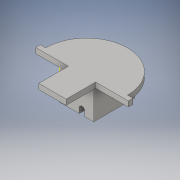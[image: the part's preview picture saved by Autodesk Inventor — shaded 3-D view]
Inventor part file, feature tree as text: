
AUTODESK INVENTOR PART (.ipt)
format: ipt  version: 2016 (Build 200138000, 138)  size: 614,912 bytes
history: native  units: in
note: dims shown in document units (in); Inventor stores cm internally (conversion verified against a paired STEP export)
features: reference x41, extrude x33, sketch x33, plane x6, projected_geometry x5
ambient origin geometry x8: Origin, YZ Plane, XZ Plane, XY Plane, X Axis, Y Axis, Z Axis, Center Point
bodies: Solid1 (feature_tree)
feature tree (118):
  extrude  "Extrusion1"  Depth=3.0in
  extrude  "Extrusion2"  Depth=0.1969in
  extrude  "Extrusion3"  Depth=1.0827in
  extrude  "Extrusion5"  Depth=1.0in TaperAngle=0.0deg
  plane  "Work Plane1"
  extrude  "Extrusion6"  Depth=0.0098in
  extrude  "Extrusion9"  Depth=0.1575in
  extrude  "Extrusion14"  Depth=0.1575in
  extrude  "Extrusion15"  Depth=1.25in
  plane  "Work Plane2"
  extrude  "Extrusion16"  Depth=0.1575in
  extrude  "Extrusion17"  Depth=0.1181in TaperAngle=0.0deg
  extrude  "Extrusion18"  Depth=0.1969in
  plane  "Work Plane3"
  extrude  "Extrusion20"  Depth=0.1969in TaperAngle=0.0deg
  extrude  "Extrusion21"  Depth=0.1181in TaperAngle=0.0deg
  plane  "Work Plane4"
  plane  "Work Plane5"
  extrude  "Extrusion23"  Depth=0.1181in
  extrude  "Extrusion24"  Depth=0.1969in TaperAngle=0.0deg
  plane  "Work Plane6"
  extrude  "Extrusion25"  Depth=0.35in
  extrude  "Extrusion26"  Depth=0.2in
  extrude  "Extrusion27"  Depth=0.1969in TaperAngle=0.0deg
  extrude  "Extrusion28"  Depth=1.5in
  extrude  "Extrusion29"  Depth=0.7in
  extrude  "Extrusion30"  Depth=0.1181in TaperAngle=0.0deg
  extrude  "Extrusion31"  Depth=1.0in
  extrude  "Extrusion34"  Depth=0.5in
  sketch  "Sketch36"  dims[d105=0.1181in d106=0.5in]
  extrude  "Extrusion35"  Depth=0.5in
  extrude  "Extrusion36"  Depth=0.0197in
  extrude  "Extrusion37"  Depth=0.325in
  extrude  "Extrusion38"  Depth=0.1969in
  extrude  "Extrusion39"  Depth=0.1181in
  sketch  "Sketch41"  dims[d117=0.1969in d118=0.1181in]
  extrude  "Extrusion41"  Depth=0.1575in TaperAngle=0.0deg
  extrude  "Extrusion42"  Depth=1.0in TaperAngle=0.0deg
  extrude  "Extrusion43"  Depth=0.5in
  extrude  "Extrusion44"  Depth=0.0039in
  extrude  "Extrusion45"  Depth=0.0394in
  sketch  "Sketch1"  dims[d0=4.5in d1=3.0in]
  sketch  "Sketch2"  dims[d2=0.1969in d3=0.0in d5=0.0787in]
  reference  "Reference1"
  reference  "Reference2"
  sketch  "Sketch3"  dims[d6=1.0in d7=0.0in d8=1.0827in]
  sketch  "Sketch5"  dims[d9=0.3937in d10=1.0in d11=0.0in]
  reference  "Reference14"
  reference  "Reference15"
  reference  "Reference16"
  reference  "Reference17"
  reference  "Reference18"
  sketch  "Sketch6"  dims[d12=0.0787in d23=0.0098in]
  reference  "Reference19"
  sketch  "Sketch9"  dims[d24=0.1575in d25=0.0787in]
  projected_geometry  "Projected Loop2"
  sketch  "Sketch14"  dims[d26=0.0098in d27=0.1575in]
  sketch  "Sketch15"  dims[d28=0.1181in d29=0.0in d30=1.25in]
  sketch  "Sketch16"  dims[d31=0.1575in d32=0.1575in]
  reference  "Reference30"
  sketch  "Sketch17"  dims[d33=0.1181in d34=0.0in d46=0.9201in d47=0.0in]
  reference  "Reference31"
  reference  "Reference32"
  reference  "Reference33"
  reference  "Reference35"
  reference  "Reference36"
  reference  "Reference37"
  reference  "Reference38"
  reference  "Reference39"
  reference  "Reference40"
  reference  "Reference41"
  reference  "Reference42"
  reference  "Reference43"
  reference  "Reference44"
  reference  "Reference45"
  reference  "Reference46"
  reference  "Reference47"
  reference  "Reference48"
  reference  "Reference49"
  sketch  "Sketch20"  dims[d58=0.1969in d59=0.1969in]
  reference  "Reference50"
  sketch  "Sketch21"  dims[d60=0.1969in d61=0.1969in d62=0.0in]
  sketch  "Sketch23"  dims[d63=1.0in d64=0.0in d65=0.1181in d66=0.0in]
  reference  "Reference53"
  reference  "Reference54"
  sketch  "Sketch24"  dims[d67=0.1969in d68=0.0in d69=0.1181in]
  sketch  "Sketch25"  dims[d70=0.1181in d71=0.1969in d72=0.0in]
  reference  "Reference55"
  reference  "Reference56"
  sketch  "Sketch26"  dims[d75=0.0394in d76=0.35in]
  reference  "Reference57"
  reference  "Reference58"
  sketch  "Sketch28"  dims[d77=0.1628in d78=0.2in]
  sketch  "Sketch29"  dims[d79=0.0787in d80=0.0in d81=0.1969in d82=0.0in]
  sketch  "Sketch30"  dims[d89=1.5in d90=1.5in]
  reference  "Reference59"
  sketch  "Sketch31"  dims[d91=0.1181in d92=0.0in d93=0.7in]
  sketch  "Sketch32"  dims[d94=1.26in d95=0.0in d96=0.1181in d97=0.0in]
  sketch  "Sketch35"  dims[d98=0.1181in d99=0.0in d104=1.0in]
  reference  "Reference61"
  sketch  "Sketch37"  dims[d107=1.0in d108=0.5in]
  reference  "Reference62"
  sketch  "Sketch38"  dims[d109=10.0in d110=0.0in d111=0.0197in]
  reference  "Reference63"
  sketch  "Sketch39"  dims[d112=0.0197in d113=0.325in]
  reference  "Reference64"
  sketch  "Sketch40"  dims[d114=0.197in d115=0.0in d116=0.1969in]
  reference  "Reference65"
  projected_geometry  "Projected Loop6"
  sketch  "Sketch42"  dims[d119=0.1969in d120=0.0in d121=0.1575in d122=0.0in]
  projected_geometry  "Projected Loop7"
  sketch  "Sketch43"  dims[d123=0.1in d124=0.0in d132=1.0in d133=0.0in]
  reference  "Reference66"
  sketch  "Sketch44"  dims[d134=0.5in d135=0.5in]
  sketch  "Sketch45"  dims[d136=0.0039in d137=0.0039in]
  projected_geometry  "Projected Loop8"
  projected_geometry  "Projected Loop9"
  sketch  "Sketch46"  dims[d138=0.0984in d139=0.0984in d140=0.0039in d141=0.0984in d142=1.61in d143=0.0in d144=0.2in d145=0.0in d146=0.1181in d147=0.85in d148=0.0in d149=1.2in d150=0.1181in d151=1.1in d152=0.0in d153=0.28in d154=3.0in d155=0.0in d158=222.0in d159=0.0in d160=0.5in d161=1.0in d162=0.2in d163=0.0in d164=0.2in d165=5.0in d166=0.0in d167=0.0394in d168=0.0in d169=0.0394in d170=111.0in d171=0.0in]
